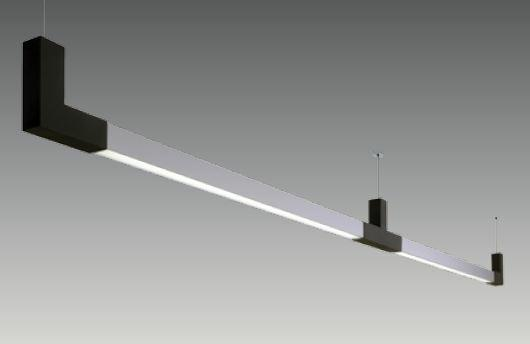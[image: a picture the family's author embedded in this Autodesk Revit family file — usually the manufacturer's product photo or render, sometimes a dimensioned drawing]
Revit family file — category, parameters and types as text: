
# Revit family: S 3000 PLT
name_source: partatom
category: Lighting Fixtures
revit_build: Autodesk Revit 2017 (Build: 20160225_1515(x64)
units: mm (PartAtom-declared; Revit-internal decimal feet)

## family parameters
Cut with Voids When Loaded = No
Host = Face
Light Source = Yes
Part Type = Normal
Room Calculation Point = No
Round Connector Dimension = Use Diameter
Shared = No

## types (2) — shared parameters
Color Filter = 16777215
Default Elevation = 1219 mm
Dimming Lamp Color Temperature Shift = <None>
Emit Shape Visible in Rendering = Yes
Emit from Rectangle Length = 40 mm  [stored 0.131234 ft]
Emit from Rectangle Width = 1130 mm  [stored 3.70735 ft]
Light Source Symbol Size = 610 mm
Manufacturer = ARLIGHT
Type Image = S 3000 PLT.JPG
Wattage Comments = 88W

## type names (no varying parameters)
- SDPLT.3000.88.30
- SDPLT.3000.88.40

note: [stored X ft] marks values corroborated as IEEE doubles in the binary element streams (Revit-internal decimal feet)

## geometry (parser evidence)
native form markers: Sweep x3
no freeform markers — native parametric forms only
